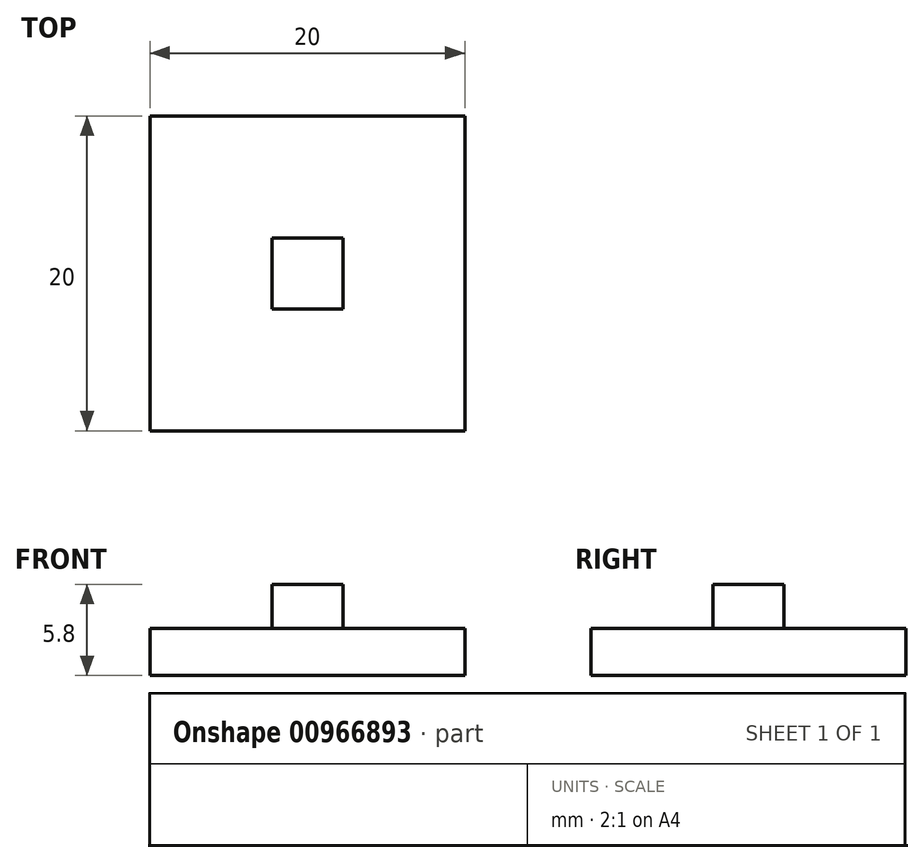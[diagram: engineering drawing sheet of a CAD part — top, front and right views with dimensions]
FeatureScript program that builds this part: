
annotation { "Feature Type Name" : "Feature", "Feature Type Description" : "" }
export const myFeature = defineFeature(function(context is Context, id is Id, definition is map)
    precondition{}
    {
        {
            var Q0;
            Q0=qCreatedBy(makeId("Top.planeOp"),FACE);
            var sketch = newSketch(context, id + "F0", { "sketchPlane" : qUnion([Q0])});
            skLineSegment(sketch, "E0.bottom", {"start": v(-10, -10) * mm, "end": v(10, -10) * mm});
            skLineSegment(sketch, "E0.top", {"start": v(-10, 10) * mm, "end": v(10, 10) * mm});
            skLineSegment(sketch, "E0.left", {"start": v(-10, -10) * mm, "end": v(-10, 10) * mm});
            skLineSegment(sketch, "E0.right", {"start": v(10, -10) * mm, "end": v(10, 10) * mm});
            skLineSegment(sketch, "E1", {"start": v(-10, 10) * mm, "end": v(10, -10) * mm, "construction": true});
            skSolve(sketch);
        }
        {
            var Q0;
            Q0 = qSketchRegion(id + "F0", true);
            extrude(context, id + "F1", {"entities" : qUnion([Q0]), "depth" : 3 * mm, "offsetDistance" : 25 * mm});
        }
        {
            var Q0;
            Q0=makeQuery(id+"F1.opExtrude","CAP_FACE",FACE,{"disambiguationData":[OSD([sQuery(id+"F0.wireOp",EDGE,"E0.bottom"),sQuery(id+"F0.wireOp",EDGE,"E0.top"),sQuery(id+"F0.wireOp",EDGE,"E0.left"),sQuery(id+"F0.wireOp",EDGE,"E0.right")])],"isStart":false});
            var sketch = newSketch(context, id + "F2", { "sketchPlane" : qUnion([Q0])});
            skLineSegment(sketch, "E2.bottom", {"start": v(-2.25, -2.25) * mm, "end": v(2.25, -2.25) * mm});
            skLineSegment(sketch, "E2.top", {"start": v(-2.25, 2.25) * mm, "end": v(2.25, 2.25) * mm});
            skLineSegment(sketch, "E2.left", {"start": v(-2.25, -2.25) * mm, "end": v(-2.25, 2.25) * mm});
            skLineSegment(sketch, "E2.right", {"start": v(2.25, -2.25) * mm, "end": v(2.25, 2.25) * mm});
            skLineSegment(sketch, "E3", {"start": v(-2.25, -2.25) * mm, "end": v(2.25, 2.25) * mm, "construction": true});
            skSolve(sketch);
        }
        {
            var Q0;
            Q0 = qSketchRegion(id + "F2", true);
            extrude(context, id + "F3", {"entities" : qUnion([Q0]), "operationType" : NewBodyOperationType.ADD, "depth" : 2.8 * mm, "offsetDistance" : 25 * mm});
        }
    });
